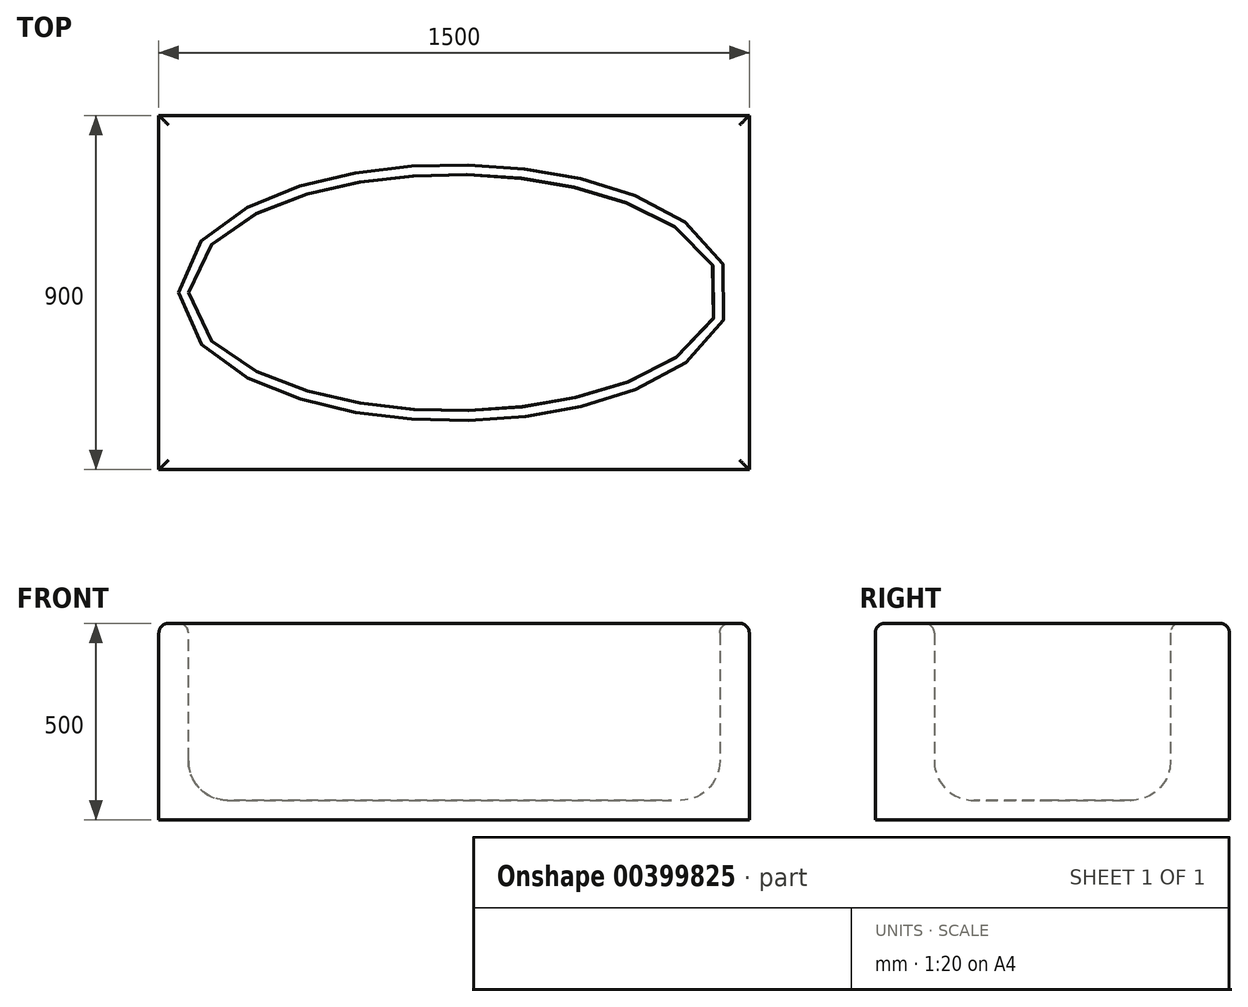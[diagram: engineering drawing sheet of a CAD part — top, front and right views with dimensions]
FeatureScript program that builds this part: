
annotation { "Feature Type Name" : "Feature", "Feature Type Description" : "" }
export const myFeature = defineFeature(function(context is Context, id is Id, definition is map)
    precondition{}
    {
        {
            var Q0;
            Q0=qCreatedBy(makeId("Top.planeOp"),FACE);
            var sketch = newSketch(context, id + "F0", { "sketchPlane" : qUnion([Q0])});
            skLineSegment(sketch, "E0.bottom", {"start": v(0, 0) * mm, "end": v(1500, 0) * mm});
            skLineSegment(sketch, "E0.top", {"start": v(0, 900) * mm, "end": v(1500, 900) * mm});
            skLineSegment(sketch, "E0.left", {"start": v(0, 0) * mm, "end": v(0, 900) * mm});
            skLineSegment(sketch, "E0.right", {"start": v(1500, 0) * mm, "end": v(1500, 900) * mm});
            skSolve(sketch);
        }
        {
            var Q0;
            Q0 = qSketchRegion(id + "F0", true);
            extrude(context, id + "F1", {"entities" : qUnion([Q0]), "depth" : 500 * mm});
        }
        {
            var Q0;
            Q0=makeQuery(id+"F1.opExtrude","CAP_FACE",FACE,{"disambiguationData":[OSD([sQuery(id+"F0.wireOp",EDGE,"E0.bottom"),sQuery(id+"F0.wireOp",EDGE,"E0.top"),sQuery(id+"F0.wireOp",EDGE,"E0.left"),sQuery(id+"F0.wireOp",EDGE,"E0.right")])],"isStart":false});
            var sketch = newSketch(context, id + "F2", { "sketchPlane" : qUnion([Q0])});
            skEllipse(sketch, "E1", {"center": v(750, 450) * mm, "majorRadius": 675 * mm, "minorRadius": 300 * mm, "majorAxis": v(-1, 0)});
            skPoint(sketch, "E1.centerSnap0", {"position": v(1500, 450) * mm});
            skPoint(sketch, "E1.centerSnap1", {"position": v(750, 0) * mm});
            skSolve(sketch);
        }
        {
            var Q0;
            Q0 = qSketchRegion(id + "F2", true);
            extrude(context, id + "F3", {"entities" : qUnion([Q0]), "operationType" : NewBodyOperationType.REMOVE, "oppositeDirection" : true, "depth" : 450 * mm});
        }
        {
            var Q0;
            Q0=makeQuery(id+"F3.boolean.opBoolean","COPY",EDGE,{"derivedFrom":makeQuery(id+"F3.opExtrude","CAP_EDGE",EDGE,{"disambiguationData":[OSD([sQuery(id+"F2.wireOp",EDGE,"E1")])],"isStart":false})});
            fillet(context, id + "F4", {"entities" : qUnion([Q0]), "radius" : 100 * mm, "tangentPropagation" : true, "allowEdgeOverflow" : false});
        }
        {
            var Q0;
            Q0=makeQuery(id+"F1.opExtrude","CAP_EDGE",EDGE,{"disambiguationData":[OSD([sQuery(id+"F0.wireOp",EDGE,"E0.bottom")])],"isStart":false});
            var Q1;
            Q1=makeQuery(id+"F1.opExtrude","CAP_FACE",FACE,{"disambiguationData":[OSD([sQuery(id+"F0.wireOp",EDGE,"E0.bottom"),sQuery(id+"F0.wireOp",EDGE,"E0.top"),sQuery(id+"F0.wireOp",EDGE,"E0.left"),sQuery(id+"F0.wireOp",EDGE,"E0.right")])],"isStart":false});
            fillet(context, id + "F5", {"entities" : qUnion([Q0, Q1]), "radius" : 25 * mm, "tangentPropagation" : true, "allowEdgeOverflow" : false});
        }
    });
